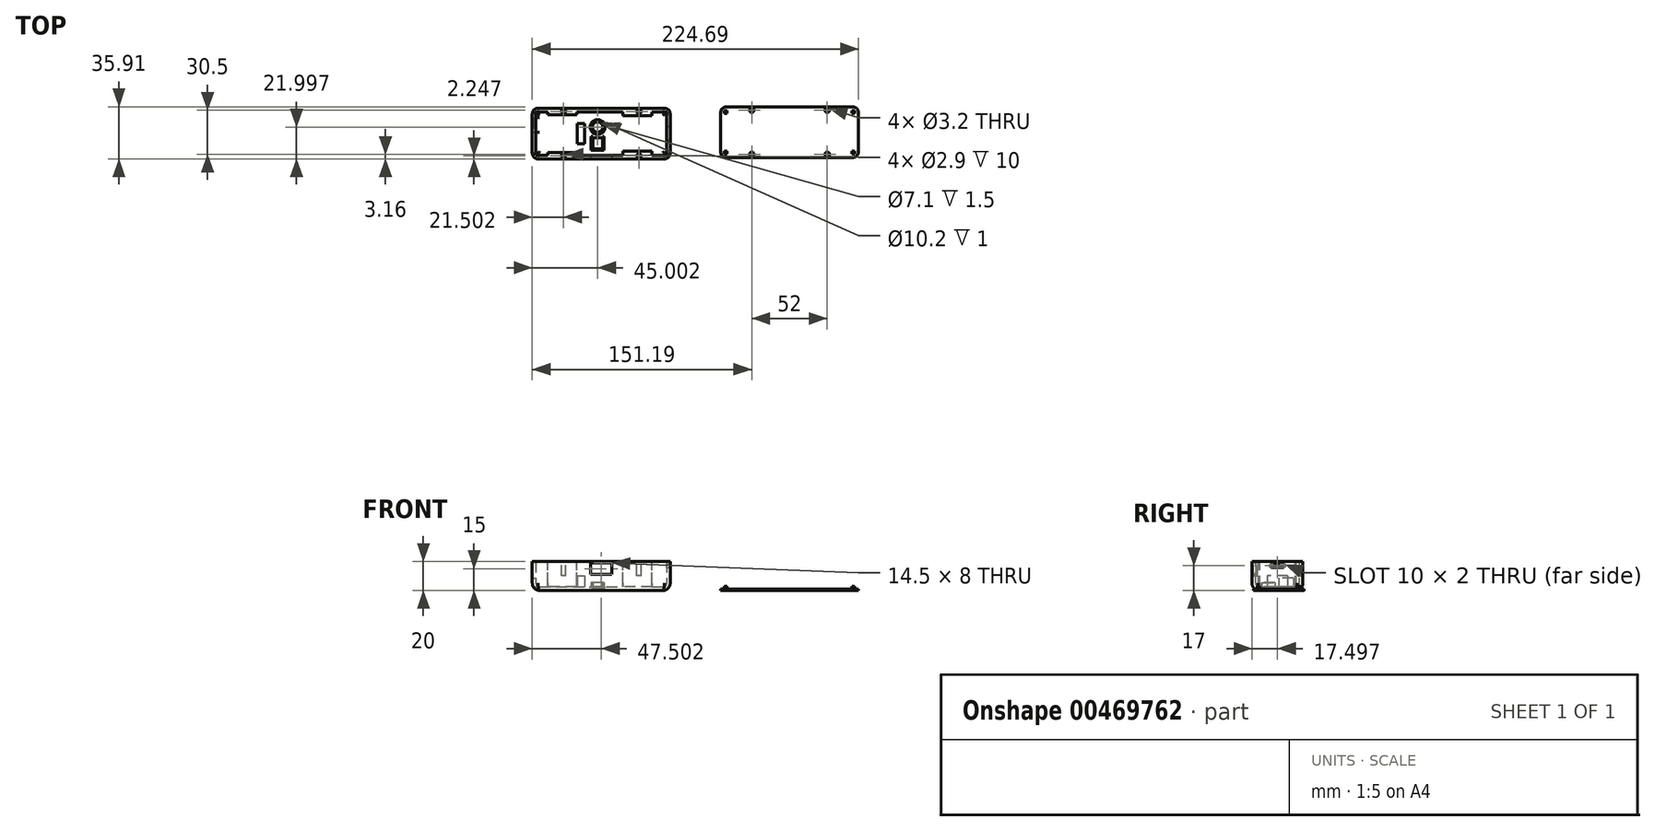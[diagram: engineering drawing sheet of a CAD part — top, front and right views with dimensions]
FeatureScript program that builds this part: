
annotation { "Feature Type Name" : "Feature", "Feature Type Description" : "" }
export const myFeature = defineFeature(function(context is Context, id is Id, definition is map)
    precondition{}
    {
        {
            var Q0;
            Q0=qCreatedBy(makeId("Top.planeOp"),FACE);
            var sketch = newSketch(context, id + "F0", { "sketchPlane" : qUnion([Q0])});
            skLineSegment(sketch, "E0.bottom", {"start": v(-57.56, 16.59) * mm, "end": v(37.44, 16.59) * mm});
            skLineSegment(sketch, "E0.top", {"start": v(-57.56, -18.41) * mm, "end": v(37.44, -18.41) * mm});
            skLineSegment(sketch, "E0.left", {"start": v(-57.56, 16.59) * mm, "end": v(-57.56, -18.41) * mm});
            skLineSegment(sketch, "E0.right", {"start": v(37.44, 16.59) * mm, "end": v(37.44, -18.41) * mm});
            skSolve(sketch);
        }
        {
            var Q0;
            Q0=makeQuery(id+"F0.imprint","IMPRINT",FACE,{"disambiguationData":[TD([[makeQuery(id+"F0.imprint","IMPRINT",EDGE,{"derivedFrom":sQuery(id+"F0.wireOp",EDGE,"E0.bottom")}),-1.0]])]});
            extrude(context, id + "F1", {"entities" : qUnion([Q0]), "depth" : 20 * mm});
        }
        {
            var Q0;
            Q0=makeQuery(id+"F1.opExtrude","CAP_FACE",FACE,{"disambiguationData":[OSD([sQuery(id+"F0.wireOp",EDGE,"E0.bottom"),sQuery(id+"F0.wireOp",EDGE,"E0.top"),sQuery(id+"F0.wireOp",EDGE,"E0.left"),sQuery(id+"F0.wireOp",EDGE,"E0.right")])],"isStart":true});
            fillet(context, id + "F2", {"entities" : qUnion([Q0]), "radius" : 5 * mm, "tangentPropagation" : true, "allowEdgeOverflow" : false});
        }
        {
            var Q0;
            Q0=makeQuery(id+"F1.opExtrude","CAP_FACE",FACE,{"disambiguationData":[OSD([sQuery(id+"F0.wireOp",EDGE,"E0.bottom"),sQuery(id+"F0.wireOp",EDGE,"E0.top"),sQuery(id+"F0.wireOp",EDGE,"E0.left"),sQuery(id+"F0.wireOp",EDGE,"E0.right")])],"isStart":false});
            shell(context, id + "F3", {"entities" : qUnion([Q0]), "thickness" : 2.5 * mm});
        }
        {
            var Q0;
            Q0=makeQuery(id+"F1.opExtrude","SWEPT_EDGE",EDGE,{"disambiguationData":[OSD([sQuery(id+"F0.wireOp",EDGE,"E0.bottom"),sQuery(id+"F0.wireOp",EDGE,"E0.left")])]});
            var Q1;
            Q1=makeQuery(id+"F1.opExtrude","SWEPT_EDGE",EDGE,{"disambiguationData":[OSD([sQuery(id+"F0.wireOp",EDGE,"E0.top"),sQuery(id+"F0.wireOp",EDGE,"E0.left")])]});
            var Q2;
            Q2=makeQuery(id+"F1.opExtrude","SWEPT_EDGE",EDGE,{"disambiguationData":[OSD([sQuery(id+"F0.wireOp",EDGE,"E0.top"),sQuery(id+"F0.wireOp",EDGE,"E0.right")])]});
            var Q3;
            Q3=makeQuery(id+"F1.opExtrude","SWEPT_EDGE",EDGE,{"disambiguationData":[OSD([sQuery(id+"F0.wireOp",EDGE,"E0.bottom"),sQuery(id+"F0.wireOp",EDGE,"E0.right")])]});
            fillet(context, id + "F4", {"entities" : qUnion([Q0, Q1, Q2, Q3]), "radius" : 4 * mm, "tangentPropagation" : true, "allowEdgeOverflow" : false});
        }
        {
            var Q0;
            Q0=makeQuery(id+"F1.opExtrude","CAP_FACE",FACE,{"disambiguationData":[OSD([sQuery(id+"F0.wireOp",EDGE,"E0.bottom"),sQuery(id+"F0.wireOp",EDGE,"E0.top"),sQuery(id+"F0.wireOp",EDGE,"E0.left"),sQuery(id+"F0.wireOp",EDGE,"E0.right")])],"isStart":false});
            var sketch = newSketch(context, id + "F5", { "sketchPlane" : qUnion([Q0])});
            skLineSegment(sketch, "E1.bottom", {"start": v(-47.06, 14.09) * mm, "end": v(-27.06, 14.09) * mm});
            skLineSegment(sketch, "E1.top", {"start": v(-47.06, 12.09) * mm, "end": v(-27.06, 12.09) * mm});
            skLineSegment(sketch, "E1.left", {"start": v(-47.06, 14.09) * mm, "end": v(-47.06, 12.09) * mm});
            skLineSegment(sketch, "E1.right", {"start": v(-27.06, 14.09) * mm, "end": v(-27.06, 12.09) * mm});
            skLineSegment(sketch, "E2.bottom", {"start": v(-47.06, -15.91) * mm, "end": v(-27.06, -15.91) * mm});
            skLineSegment(sketch, "E2.top", {"start": v(-47.06, -13.91) * mm, "end": v(-27.06, -13.91) * mm});
            skLineSegment(sketch, "E2.left", {"start": v(-47.06, -15.91) * mm, "end": v(-47.06, -13.91) * mm});
            skLineSegment(sketch, "E2.right", {"start": v(-27.06, -15.91) * mm, "end": v(-27.06, -13.91) * mm});
            skLineSegment(sketch, "E3.bottom", {"start": v(4.94, 14.09) * mm, "end": v(24.94, 14.09) * mm});
            skLineSegment(sketch, "E3.top", {"start": v(4.94, 11.34) * mm, "end": v(24.94, 11.34) * mm});
            skLineSegment(sketch, "E3.left", {"start": v(4.94, 14.09) * mm, "end": v(4.94, 11.34) * mm});
            skLineSegment(sketch, "E3.right", {"start": v(24.94, 14.09) * mm, "end": v(24.94, 11.34) * mm});
            skLineSegment(sketch, "E4.bottom", {"start": v(4.94, -15.91) * mm, "end": v(24.94, -15.91) * mm});
            skLineSegment(sketch, "E4.top", {"start": v(4.94, -13.16) * mm, "end": v(24.94, -13.16) * mm});
            skLineSegment(sketch, "E4.left", {"start": v(4.94, -15.91) * mm, "end": v(4.94, -13.16) * mm});
            skLineSegment(sketch, "E4.right", {"start": v(24.94, -15.91) * mm, "end": v(24.94, -13.16) * mm});
            skSolve(sketch);
        }
        {
            var Q0;
            Q0=makeQuery(id+"F5.imprint","IMPRINT",FACE,{"disambiguationData":[TD([[makeQuery(id+"F5.imprint","IMPRINT",EDGE,{"derivedFrom":sQuery(id+"F5.wireOp",EDGE,"E1.bottom")}),-1.0]])]});
            var Q1;
            Q1=makeQuery(id+"F5.imprint","IMPRINT",FACE,{"disambiguationData":[TD([[makeQuery(id+"F5.imprint","IMPRINT",EDGE,{"derivedFrom":sQuery(id+"F5.wireOp",EDGE,"E2.bottom")}),1.0]])]});
            var Q2;
            Q2=makeQuery(id+"F5.imprint","IMPRINT",FACE,{"disambiguationData":[TD([[makeQuery(id+"F5.imprint","IMPRINT",EDGE,{"derivedFrom":sQuery(id+"F5.wireOp",EDGE,"E4.bottom")}),1.0]])]});
            var Q3;
            Q3=makeQuery(id+"F5.imprint","IMPRINT",FACE,{"disambiguationData":[TD([[makeQuery(id+"F5.imprint","IMPRINT",EDGE,{"derivedFrom":sQuery(id+"F5.wireOp",EDGE,"E3.bottom")}),-1.0]])]});
            extrude(context, id + "F6", {"entities" : qUnion([Q0, Q1, Q2, Q3]), "operationType" : NewBodyOperationType.ADD, "endBound" : BoundingType.UP_TO_NEXT, "oppositeDirection" : true, "depth" : 25 * mm});
        }
        {
            var Q0;
            Q0=makeQuery(id+"F3.opShell","OFFSET_FACE",FACE,{"disambiguationData":[OSD([sQuery(id+"F0.wireOp",EDGE,"E0.bottom"),sQuery(id+"F0.wireOp",EDGE,"E0.top"),sQuery(id+"F0.wireOp",EDGE,"E0.left"),sQuery(id+"F0.wireOp",EDGE,"E0.right")])]});
            var sketch = newSketch(context, id + "F7", { "sketchPlane" : qUnion([Q0])});
            skLineSegment(sketch, "E5", {"start": v(-12.56, 11.59) * mm, "end": v(-12.56, -13.41) * mm, "construction": true});
            skCircle(sketch, "E6", {"center": v(-12.56, 3.59) * mm, "radius": 3.55 * mm});
            skLineSegment(sketch, "E7.bottom", {"start": v(-9.16, -11.41) * mm, "end": v(-15.96, -11.41) * mm});
            skLineSegment(sketch, "E7.top", {"start": v(-9.16, -3.71) * mm, "end": v(-15.96, -3.71) * mm});
            skLineSegment(sketch, "E7.left", {"start": v(-9.16, -11.41) * mm, "end": v(-9.16, -3.71) * mm});
            skLineSegment(sketch, "E7.right", {"start": v(-15.96, -11.41) * mm, "end": v(-15.96, -3.71) * mm});
            skPoint(sketch, "E7.middle", {"position": v(-12.56, -7.56) * mm});
            skLineSegment(sketch, "E8.bottom", {"start": v(-8.16, -2.71) * mm, "end": v(-9.16, -2.71) * mm});
            skLineSegment(sketch, "E8.top", {"start": v(-8.16, -12.41) * mm, "end": v(-16.96, -12.41) * mm});
            skLineSegment(sketch, "E8.left", {"start": v(-8.16, -2.71) * mm, "end": v(-8.16, -12.41) * mm});
            skLineSegment(sketch, "E8.right", {"start": v(-16.96, -2.71) * mm, "end": v(-16.96, -12.41) * mm});
            skLineSegment(sketch, "E9", {"start": v(-15.96, -3.71) * mm, "end": v(-15.96, -2.71) * mm});
            skLineSegment(sketch, "E10", {"start": v(-9.16, -3.71) * mm, "end": v(-9.16, -2.71) * mm});
            skLineSegment(sketch, "E11.trimOffspring", {"start": v(-15.96, -2.71) * mm, "end": v(-16.96, -2.71) * mm});
            skCircle(sketch, "E12", {"center": v(-12.56, 3.59) * mm, "radius": 5.1 * mm});
            skLineSegment(sketch, "E13.bottom", {"start": v(-26.56, 6.09) * mm, "end": v(-21.56, 6.09) * mm});
            skLineSegment(sketch, "E13.top", {"start": v(-26.56, -7.91) * mm, "end": v(-21.56, -7.91) * mm});
            skLineSegment(sketch, "E13.left", {"start": v(-26.56, 6.09) * mm, "end": v(-26.56, -7.91) * mm});
            skLineSegment(sketch, "E13.right", {"start": v(-21.56, 6.09) * mm, "end": v(-21.56, -7.91) * mm});
            skPoint(sketch, "E14", {"position": v(-26.56, -0.91) * mm});
            skPoint(sketch, "E15", {"position": v(-21.56, -0.91) * mm});
            skLineSegment(sketch, "E16", {"start": v(-52.56, -0.91) * mm, "end": v(-26.56, -0.91) * mm, "construction": true});
            skSolve(sketch);
        }
        {
            var Q0;
            Q0=makeQuery(id+"F7.imprint","IMPRINT",FACE,{"disambiguationData":[TD([[makeQuery(id+"F7.imprint","IMPRINT",EDGE,{"derivedFrom":sQuery(id+"F7.wireOp",EDGE,"E6")}),1.0]])]});
            var Q1;
            Q1=makeQuery(id+"F7.imprint","IMPRINT",FACE,{"disambiguationData":[TD([[makeQuery(id+"F7.imprint","IMPRINT",EDGE,{"derivedFrom":sQuery(id+"F7.wireOp",EDGE,"E7.bottom")}),-1.0]])]});
            extrude(context, id + "F8", {"entities" : qUnion([Q0, Q1]), "operationType" : NewBodyOperationType.REMOVE, "endBound" : BoundingType.UP_TO_NEXT, "oppositeDirection" : true, "depth" : 25 * mm});
        }
        {
            var Q0;
            Q0=makeQuery(id+"F7.imprint","IMPRINT",FACE,{"disambiguationData":[TD([[makeQuery(id+"F7.imprint","IMPRINT",EDGE,{"derivedFrom":sQuery(id+"F7.wireOp",EDGE,"E6")}),-1.0]])]});
            extrude(context, id + "F9", {"entities" : qUnion([Q0]), "operationType" : NewBodyOperationType.REMOVE, "oppositeDirection" : true, "depth" : 1 * mm});
        }
        {
            var Q0;
            Q0=makeQuery(id+"F7.imprint","IMPRINT",FACE,{"disambiguationData":[TD([[makeQuery(id+"F7.imprint","IMPRINT",EDGE,{"derivedFrom":sQuery(id+"F7.wireOp",EDGE,"E7.bottom")}),1.0]])]});
            extrude(context, id + "F10", {"entities" : qUnion([Q0]), "operationType" : NewBodyOperationType.ADD, "depth" : 3 * mm});
        }
        {
            var Q0;
            Q0=makeQuery(id+"F7.imprint","IMPRINT",FACE,{"disambiguationData":[TD([[makeQuery(id+"F7.imprint","IMPRINT",EDGE,{"derivedFrom":sQuery(id+"F7.wireOp",EDGE,"E13.bottom")}),-1.0]])]});
            extrude(context, id + "F11", {"entities" : qUnion([Q0]), "operationType" : NewBodyOperationType.ADD, "depth" : 7.6 * mm});
        }
        {
            var Q0;
            Q0=makeQuery(id+"F6.opExtrude","SWEPT_FACE",FACE,{"disambiguationData":[OSD([sQuery(id+"F5.wireOp",EDGE,"E1.left")])]});
            var sketch = newSketch(context, id + "F12", { "sketchPlane" : qUnion([Q0])});
            skLineSegment(sketch, "E17.bottom", {"start": v(-10.09, 8.5) * mm, "end": v(-0.09, 8.5) * mm});
            skLineSegment(sketch, "E17.top", {"start": v(-10.09, 2.5) * mm, "end": v(-0.09, 2.5) * mm});
            skLineSegment(sketch, "E17.left", {"start": v(-10.09, 8.5) * mm, "end": v(-10.09, 2.5) * mm});
            skLineSegment(sketch, "E17.right", {"start": v(-0.09, 8.5) * mm, "end": v(-0.09, 2.5) * mm});
            skSolve(sketch);
        }
        {
            var Q0;
            Q0=makeQuery(id+"F12.imprint","IMPRINT",FACE,{"disambiguationData":[TD([[makeQuery(id+"F12.imprint","IMPRINT",EDGE,{"derivedFrom":sQuery(id+"F12.wireOp",EDGE,"E17.bottom")}),-1.0]])]});
            extrude(context, id + "F13", {"entities" : qUnion([Q0]), "operationType" : NewBodyOperationType.REMOVE, "depth" : 13.3 * mm});
        }
        {
            var Q0;
            Q0=makeQuery(id+"F1.opExtrude","SWEPT_FACE",FACE,{"disambiguationData":[OSD([sQuery(id+"F0.wireOp",EDGE,"E0.right")])]});
            var sketch = newSketch(context, id + "F14", { "sketchPlane" : qUnion([Q0])});
            skLineSegment(sketch, "E18", {"start": v(12.59, 17) * mm, "end": v(-14.41, 17) * mm, "construction": true});
            skArc(sketch, "E19", {"start": v(3.09, 16) * mm, "mid": v(4.09, 17) * mm, "end": v(3.09, 18) * mm});
            skArc(sketch, "E20", {"start": v(-4.91, 18) * mm, "mid": v(-5.91, 16.97) * mm, "end": v(-4.86, 16) * mm});
            skLineSegment(sketch, "E21", {"start": v(3.09, 18) * mm, "end": v(-4.91, 18) * mm});
            skLineSegment(sketch, "E22", {"start": v(-4.97, 16) * mm, "end": v(3.09, 16) * mm});
            skLineSegment(sketch, "E23", {"start": v(-0.91, 18) * mm, "end": v(-0.91, 20) * mm, "construction": true});
            skSolve(sketch);
        }
        {
            var Q0;
            {var subQ5=sQuery(id+"F14.wireOp",EDGE,"E19");Q0=makeQuery(id+"F14.imprint","IMPRINT",FACE,{"disambiguationData":[TD([[makeQuery(id+"F14.imprint","IMPRINT",EDGE,{"derivedFrom":subQ5}),1.0]])]});}
            extrude(context, id + "F15", {"entities" : qUnion([Q0]), "operationType" : NewBodyOperationType.REMOVE, "endBound" : BoundingType.UP_TO_NEXT, "oppositeDirection" : true, "depth" : 25 * mm});
        }
        {
            var Q0;
            Q0=makeQuery(id+"F6.boolean.opBoolean","MERGE",FACE,{"derivedFrom":[makeQuery(id+"F1.opExtrude","CAP_FACE",FACE,{"disambiguationData":[OSD([sQuery(id+"F0.wireOp",EDGE,"E0.bottom"),sQuery(id+"F0.wireOp",EDGE,"E0.top"),sQuery(id+"F0.wireOp",EDGE,"E0.left"),sQuery(id+"F0.wireOp",EDGE,"E0.right")])],"isStart":false}),makeQuery(id+"F6.opExtrude","CAP_FACE",FACE,{"disambiguationData":[OSD([sQuery(id+"F5.wireOp",EDGE,"E1.bottom"),sQuery(id+"F5.wireOp",EDGE,"E1.top"),sQuery(id+"F5.wireOp",EDGE,"E1.left"),sQuery(id+"F5.wireOp",EDGE,"E1.right")])],"isStart":true}),makeQuery(id+"F6.opExtrude","CAP_FACE",FACE,{"disambiguationData":[OSD([sQuery(id+"F5.wireOp",EDGE,"E2.bottom"),sQuery(id+"F5.wireOp",EDGE,"E2.top"),sQuery(id+"F5.wireOp",EDGE,"E2.left"),sQuery(id+"F5.wireOp",EDGE,"E2.right")])],"isStart":true}),makeQuery(id+"F6.opExtrude","CAP_FACE",FACE,{"disambiguationData":[OSD([sQuery(id+"F5.wireOp",EDGE,"E3.bottom"),sQuery(id+"F5.wireOp",EDGE,"E3.top"),sQuery(id+"F5.wireOp",EDGE,"E3.left"),sQuery(id+"F5.wireOp",EDGE,"E3.right")])],"isStart":true}),makeQuery(id+"F6.opExtrude","CAP_FACE",FACE,{"disambiguationData":[OSD([sQuery(id+"F5.wireOp",EDGE,"E4.bottom"),sQuery(id+"F5.wireOp",EDGE,"E4.top"),sQuery(id+"F5.wireOp",EDGE,"E4.left"),sQuery(id+"F5.wireOp",EDGE,"E4.right")])],"isStart":true})]});
            var sketch = newSketch(context, id + "F16", { "sketchPlane" : qUnion([Q0])});
            skCircle(sketch, "E24", {"center": v(-36.06, 14.34) * mm, "radius": 1.45 * mm});
            skCircle(sketch, "E25", {"center": v(-36.06, -16.16) * mm, "radius": 1.45 * mm});
            skCircle(sketch, "E26", {"center": v(15.94, -16.16) * mm, "radius": 1.45 * mm});
            skCircle(sketch, "E27", {"center": v(15.94, 14.34) * mm, "radius": 1.45 * mm});
            skLineSegment(sketch, "E28", {"start": v(-36.06, 14.34) * mm, "end": v(-36.06, -16.16) * mm, "construction": true});
            skLineSegment(sketch, "E29", {"start": v(15.94, 14.34) * mm, "end": v(15.94, -16.16) * mm, "construction": true});
            skLineSegment(sketch, "E30", {"start": v(-10.06, 16.59) * mm, "end": v(-10.06, -18.41) * mm, "construction": true});
            skLineSegment(sketch, "E31", {"start": v(-36.06, 14.34) * mm, "end": v(15.94, 14.34) * mm, "construction": true});
            skLineSegment(sketch, "E32", {"start": v(-36.06, -16.16) * mm, "end": v(15.94, -16.16) * mm, "construction": true});
            skLineSegment(sketch, "E33", {"start": v(-36.06, 14.34) * mm, "end": v(-36.06, 16.59) * mm, "construction": true});
            skLineSegment(sketch, "E34", {"start": v(-36.06, -16.16) * mm, "end": v(-36.06, -18.41) * mm, "construction": true});
            skSolve(sketch);
        }
        {
            var Q0;
            Q0=makeQuery(id+"F16.imprint","IMPRINT",FACE,{"disambiguationData":[TD([[makeQuery(id+"F16.imprint","IMPRINT",EDGE,{"derivedFrom":sQuery(id+"F16.wireOp",EDGE,"E24")}),1.0]])]});
            var Q1;
            Q1=makeQuery(id+"F16.imprint","IMPRINT",FACE,{"disambiguationData":[TD([[makeQuery(id+"F16.imprint","IMPRINT",EDGE,{"derivedFrom":sQuery(id+"F16.wireOp",EDGE,"E25")}),1.0]])]});
            var Q2;
            Q2=makeQuery(id+"F16.imprint","IMPRINT",FACE,{"disambiguationData":[TD([[makeQuery(id+"F16.imprint","IMPRINT",EDGE,{"derivedFrom":sQuery(id+"F16.wireOp",EDGE,"E26")}),1.0]])]});
            var Q3;
            Q3=makeQuery(id+"F16.imprint","IMPRINT",FACE,{"disambiguationData":[TD([[makeQuery(id+"F16.imprint","IMPRINT",EDGE,{"derivedFrom":sQuery(id+"F16.wireOp",EDGE,"E27")}),1.0]])]});
            extrude(context, id + "F17", {"entities" : qUnion([Q0, Q1, Q2, Q3]), "operationType" : NewBodyOperationType.REMOVE, "oppositeDirection" : true, "depth" : 10 * mm});
        }
        {
            var Q0;
            Q0=makeQuery(id+"F1.opExtrude","SWEPT_FACE",FACE,{"disambiguationData":[OSD([sQuery(id+"F0.wireOp",EDGE,"E0.top")])]});
            var sketch = newSketch(context, id + "F18", { "sketchPlane" : qUnion([Q0])});
            skLineSegment(sketch, "E35", {"start": v(-10.06, 20) * mm, "end": v(-10.06, 5) * mm, "construction": true});
            skLineSegment(sketch, "E36.bottom", {"start": v(-2.8, 19) * mm, "end": v(-17.3, 19) * mm});
            skLineSegment(sketch, "E36.top", {"start": v(-2.8, 11) * mm, "end": v(-17.3, 11) * mm});
            skLineSegment(sketch, "E36.left", {"start": v(-2.8, 19) * mm, "end": v(-2.8, 11) * mm});
            skLineSegment(sketch, "E36.right", {"start": v(-17.3, 19) * mm, "end": v(-17.3, 11) * mm});
            skPoint(sketch, "E36.middle", {"position": v(-10.06, 15) * mm});
            skSolve(sketch);
        }
        {
            var Q0;
            Q0=qSketchRegion(id+"F18",true);
            extrude(context, id + "F19", {"entities" : qUnion([Q0]), "operationType" : NewBodyOperationType.REMOVE, "endBound" : BoundingType.UP_TO_NEXT, "oppositeDirection" : true, "depth" : 25 * mm});
        }
        {
            var Q0;
            Q0=qCreatedBy(makeId("Top.planeOp"),FACE);
            var sketch = newSketch(context, id + "F20", { "sketchPlane" : qUnion([Q0])});
            skLineSegment(sketch, "E37.bottom", {"start": v(76.13, 17.5) * mm, "end": v(163.13, 17.5) * mm});
            skLineSegment(sketch, "E37.top", {"start": v(76.13, -17.5) * mm, "end": v(163.13, -17.5) * mm});
            skLineSegment(sketch, "E37.left", {"start": v(72.13, 13.5) * mm, "end": v(72.13, -13.5) * mm});
            skLineSegment(sketch, "E37.right", {"start": v(167.13, 13.5) * mm, "end": v(167.13, -13.5) * mm});
            skPoint(sketch, "E37.middle", {"position": v(119.63, 0) * mm});
            skPoint(sketch, "E38.visualSharp", {"position": v(72.13, 17.5) * mm});
            skArc(sketch, "E38.filletArc", {"start": v(76.13, 17.5) * mm, "mid": v(73.3, 16.33) * mm, "end": v(72.13, 13.5) * mm});
            skPoint(sketch, "E39.visualSharp", {"position": v(72.13, -17.5) * mm});
            skArc(sketch, "E39.filletArc", {"start": v(72.13, -13.5) * mm, "mid": v(73.3, -16.33) * mm, "end": v(76.13, -17.5) * mm});
            skPoint(sketch, "E40.visualSharp", {"position": v(167.13, -17.5) * mm});
            skArc(sketch, "E40.filletArc", {"start": v(163.13, -17.5) * mm, "mid": v(165.96, -16.33) * mm, "end": v(167.13, -13.5) * mm});
            skPoint(sketch, "E41.visualSharp", {"position": v(167.13, 17.5) * mm});
            skArc(sketch, "E41.filletArc", {"start": v(167.13, 13.5) * mm, "mid": v(165.96, 16.33) * mm, "end": v(163.13, 17.5) * mm});
            skSolve(sketch);
        }
        {
            var Q0;
            Q0=makeQuery(id+"F20.imprint","IMPRINT",FACE,{"disambiguationData":[TD([[makeQuery(id+"F20.imprint","IMPRINT",EDGE,{"derivedFrom":sQuery(id+"F20.wireOp",EDGE,"E37.bottom")}),-1.0]])]});
            extrude(context, id + "F21", {"entities" : qUnion([Q0]), "depth" : 1 * mm});
        }
        {
            var Q0;
            Q0=makeQuery(id+"F21.opExtrude","CAP_FACE",FACE,{"disambiguationData":[OSD([sQuery(id+"F20.wireOp",EDGE,"E37.bottom"),sQuery(id+"F20.wireOp",EDGE,"E37.top"),sQuery(id+"F20.wireOp",EDGE,"E37.left"),sQuery(id+"F20.wireOp",EDGE,"E37.right"),sQuery(id+"F20.wireOp",EDGE,"E38.filletArc"),sQuery(id+"F20.wireOp",EDGE,"E39.filletArc"),sQuery(id+"F20.wireOp",EDGE,"E40.filletArc"),sQuery(id+"F20.wireOp",EDGE,"E41.filletArc")])],"isStart":false});
            var sketch = newSketch(context, id + "F22", { "sketchPlane" : qUnion([Q0])});
            skLineSegment(sketch, "E42.bottom", {"start": v(74.73, 14.9) * mm, "end": v(76.73, 14.9) * mm});
            skLineSegment(sketch, "E42.top", {"start": v(74.73, 12.9) * mm, "end": v(76.73, 12.9) * mm});
            skLineSegment(sketch, "E42.left", {"start": v(74.73, 14.9) * mm, "end": v(74.73, 12.9) * mm});
            skLineSegment(sketch, "E42.right", {"start": v(76.73, 14.9) * mm, "end": v(76.73, 12.9) * mm});
            skLineSegment(sketch, "E43.bottom", {"start": v(74.73, -14.9) * mm, "end": v(76.73, -14.9) * mm});
            skLineSegment(sketch, "E43.top", {"start": v(74.73, -12.9) * mm, "end": v(76.73, -12.9) * mm});
            skLineSegment(sketch, "E43.left", {"start": v(74.73, -14.9) * mm, "end": v(74.73, -12.9) * mm});
            skLineSegment(sketch, "E43.right", {"start": v(76.73, -14.9) * mm, "end": v(76.73, -12.9) * mm});
            skLineSegment(sketch, "E44.bottom", {"start": v(164.53, -14.9) * mm, "end": v(162.53, -14.9) * mm});
            skLineSegment(sketch, "E44.top", {"start": v(164.53, -12.9) * mm, "end": v(162.53, -12.9) * mm});
            skLineSegment(sketch, "E44.left", {"start": v(164.53, -14.9) * mm, "end": v(164.53, -12.9) * mm});
            skLineSegment(sketch, "E44.right", {"start": v(162.53, -14.9) * mm, "end": v(162.53, -12.9) * mm});
            skLineSegment(sketch, "E45.bottom", {"start": v(164.53, 14.9) * mm, "end": v(162.53, 14.9) * mm});
            skLineSegment(sketch, "E45.top", {"start": v(164.53, 12.9) * mm, "end": v(162.53, 12.9) * mm});
            skLineSegment(sketch, "E45.left", {"start": v(164.53, 14.9) * mm, "end": v(164.53, 12.9) * mm});
            skLineSegment(sketch, "E45.right", {"start": v(162.53, 14.9) * mm, "end": v(162.53, 12.9) * mm});
            skLineSegment(sketch, "E46", {"start": v(76.73, 14.9) * mm, "end": v(162.53, 14.9) * mm, "construction": true});
            skLineSegment(sketch, "E47", {"start": v(76.73, -14.9) * mm, "end": v(162.53, -14.9) * mm, "construction": true});
            skLineSegment(sketch, "E48", {"start": v(74.73, 12.9) * mm, "end": v(74.73, -12.9) * mm, "construction": true});
            skLineSegment(sketch, "E49", {"start": v(164.53, 12.9) * mm, "end": v(164.53, -12.9) * mm, "construction": true});
            skSolve(sketch);
        }
        {
            var Q0;
            Q0=makeQuery(id+"F22.imprint","IMPRINT",FACE,{"disambiguationData":[TD([[makeQuery(id+"F22.imprint","IMPRINT",EDGE,{"derivedFrom":sQuery(id+"F22.wireOp",EDGE,"E42.bottom")}),-1.0]])]});
            var Q1;
            Q1=makeQuery(id+"F22.imprint","IMPRINT",FACE,{"disambiguationData":[TD([[makeQuery(id+"F22.imprint","IMPRINT",EDGE,{"derivedFrom":sQuery(id+"F22.wireOp",EDGE,"E43.bottom")}),1.0]])]});
            var Q2;
            Q2=makeQuery(id+"F22.imprint","IMPRINT",FACE,{"disambiguationData":[TD([[makeQuery(id+"F22.imprint","IMPRINT",EDGE,{"derivedFrom":sQuery(id+"F22.wireOp",EDGE,"E44.bottom")}),-1.0]])]});
            var Q3;
            Q3=makeQuery(id+"F22.imprint","IMPRINT",FACE,{"disambiguationData":[TD([[makeQuery(id+"F22.imprint","IMPRINT",EDGE,{"derivedFrom":sQuery(id+"F22.wireOp",EDGE,"E45.bottom")}),1.0]])]});
            extrude(context, id + "F23", {"entities" : qUnion([Q0, Q1, Q2, Q3]), "operationType" : NewBodyOperationType.ADD, "depth" : 2 * mm});
        }
        {
            var Q0;
            Q0=makeQuery(id+"F21.opExtrude","CAP_FACE",FACE,{"disambiguationData":[OSD([sQuery(id+"F20.wireOp",EDGE,"E37.bottom"),sQuery(id+"F20.wireOp",EDGE,"E37.top"),sQuery(id+"F20.wireOp",EDGE,"E37.left"),sQuery(id+"F20.wireOp",EDGE,"E37.right"),sQuery(id+"F20.wireOp",EDGE,"E38.filletArc"),sQuery(id+"F20.wireOp",EDGE,"E39.filletArc"),sQuery(id+"F20.wireOp",EDGE,"E40.filletArc"),sQuery(id+"F20.wireOp",EDGE,"E41.filletArc")])],"isStart":false});
            var sketch = newSketch(context, id + "F24", { "sketchPlane" : qUnion([Q0])});
            skLineSegment(sketch, "E50", {"start": v(119.63, 17.5) * mm, "end": v(119.63, -17.5) * mm, "construction": true});
            skLineSegment(sketch, "E51", {"start": v(93.63, 15.25) * mm, "end": v(145.63, 15.25) * mm, "construction": true});
            skLineSegment(sketch, "E52", {"start": v(145.63, 15.25) * mm, "end": v(145.63, -15.25) * mm, "construction": true});
            skLineSegment(sketch, "E53", {"start": v(145.63, -15.25) * mm, "end": v(93.63, -15.25) * mm, "construction": true});
            skLineSegment(sketch, "E54", {"start": v(93.63, -15.25) * mm, "end": v(93.63, 15.25) * mm, "construction": true});
            skCircle(sketch, "E55", {"center": v(93.63, 15.25) * mm, "radius": 1.6 * mm});
            skCircle(sketch, "E56", {"center": v(93.63, -15.25) * mm, "radius": 1.6 * mm});
            skCircle(sketch, "E57", {"center": v(145.63, -15.25) * mm, "radius": 1.6 * mm});
            skCircle(sketch, "E58", {"center": v(145.63, 15.25) * mm, "radius": 1.6 * mm});
            skLineSegment(sketch, "E59", {"start": v(93.63, 15.25) * mm, "end": v(93.63, 17.5) * mm, "construction": true});
            skLineSegment(sketch, "E60", {"start": v(93.63, -15.25) * mm, "end": v(93.63, -17.5) * mm, "construction": true});
            skSolve(sketch);
        }
        {
            var Q0;
            Q0=makeQuery(id+"F24.imprint","IMPRINT",FACE,{"disambiguationData":[TD([[makeQuery(id+"F24.imprint","IMPRINT",EDGE,{"derivedFrom":sQuery(id+"F24.wireOp",EDGE,"E55")}),1.0]])]});
            var Q1;
            Q1=makeQuery(id+"F24.imprint","IMPRINT",FACE,{"disambiguationData":[TD([[makeQuery(id+"F24.imprint","IMPRINT",EDGE,{"derivedFrom":sQuery(id+"F24.wireOp",EDGE,"E56")}),1.0]])]});
            var Q2;
            Q2=makeQuery(id+"F24.imprint","IMPRINT",FACE,{"disambiguationData":[TD([[makeQuery(id+"F24.imprint","IMPRINT",EDGE,{"derivedFrom":sQuery(id+"F24.wireOp",EDGE,"E57")}),1.0]])]});
            var Q3;
            Q3=makeQuery(id+"F24.imprint","IMPRINT",FACE,{"disambiguationData":[TD([[makeQuery(id+"F24.imprint","IMPRINT",EDGE,{"derivedFrom":sQuery(id+"F24.wireOp",EDGE,"E58")}),1.0]])]});
            extrude(context, id + "F25", {"entities" : qUnion([Q0, Q1, Q2, Q3]), "operationType" : NewBodyOperationType.REMOVE, "endBound" : BoundingType.UP_TO_NEXT, "oppositeDirection" : true, "depth" : 25 * mm});
        }
    });
